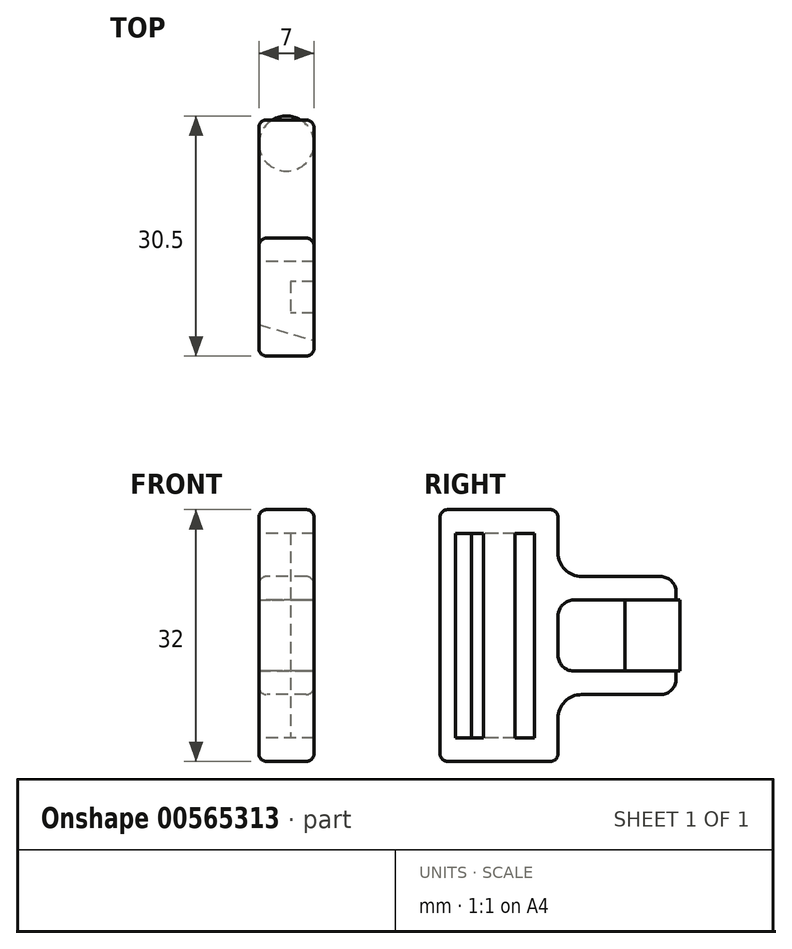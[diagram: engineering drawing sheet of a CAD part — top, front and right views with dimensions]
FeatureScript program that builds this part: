
annotation { "Feature Type Name" : "Feature", "Feature Type Description" : "" }
export const myFeature = defineFeature(function(context is Context, id is Id, definition is map)
    precondition{}
    {
        {
            var Q0;
            Q0=qCreatedBy(makeId("Right.planeOp"),FACE);
            var sketch = newSketch(context, id + "F0", { "sketchPlane" : qUnion([Q0])});
            skLineSegment(sketch, "E0.bottom", {"start": v(3, 4.5) * mm, "end": v(-12, 4.5) * mm});
            skLineSegment(sketch, "E0.top", {"start": v(3, 7.5) * mm, "end": v(-12, 7.5) * mm});
            skLineSegment(sketch, "E0.left", {"start": v(3, 4.5) * mm, "end": v(3, 7.5) * mm});
            skLineSegment(sketch, "E0.right", {"start": v(-12, 4.5) * mm, "end": v(-12, 7.5) * mm});
            skLineSegment(sketch, "E1.bottom", {"start": v(3, -4.5) * mm, "end": v(-12, -4.5) * mm});
            skLineSegment(sketch, "E1.top", {"start": v(3, -7.5) * mm, "end": v(-12, -7.5) * mm});
            skLineSegment(sketch, "E1.left", {"start": v(3, -4.5) * mm, "end": v(3, -7.5) * mm});
            skLineSegment(sketch, "E1.right", {"start": v(-12, -4.5) * mm, "end": v(-12, -7.5) * mm});
            skLineSegment(sketch, "E2.bottom", {"start": v(-12, 16) * mm, "end": v(-27, 16) * mm});
            skLineSegment(sketch, "E2.top", {"start": v(-12, -16) * mm, "end": v(-27, -16) * mm});
            skLineSegment(sketch, "E2.left", {"start": v(-12, 16) * mm, "end": v(-12, -16) * mm});
            skLineSegment(sketch, "E2.right", {"start": v(-27, 16) * mm, "end": v(-27, -16) * mm});
            skLineSegment(sketch, "E3.bottom", {"start": v(-15, 13) * mm, "end": v(-17.5, 13) * mm});
            skLineSegment(sketch, "E3.top", {"start": v(-15, -13) * mm, "end": v(-17.5, -13) * mm});
            skLineSegment(sketch, "E3.left", {"start": v(-15, 13) * mm, "end": v(-15, -13) * mm});
            skLineSegment(sketch, "E3.right", {"start": v(-17.5, 13) * mm, "end": v(-17.5, -13) * mm});
            skPoint(sketch, "E4", {"position": v(-12, 0) * mm});
            skPoint(sketch, "E5", {"position": v(-15, 0) * mm});
            skLineSegment(sketch, "E6", {"start": v(0, 4.5) * mm, "end": v(0, -4.5) * mm, "construction": true});
            skPoint(sketch, "E7", {"position": v(0, 0) * mm});
            skLineSegment(sketch, "E8.bottom", {"start": v(-21.5, 13) * mm, "end": v(-23, 13) * mm});
            skLineSegment(sketch, "E8.top", {"start": v(-21.5, -13) * mm, "end": v(-23, -13) * mm});
            skLineSegment(sketch, "E8.left", {"start": v(-21.5, 13) * mm, "end": v(-21.5, -13) * mm});
            skLineSegment(sketch, "E8.right", {"start": v(-23, 13) * mm, "end": v(-23, -13) * mm});
            skSolve(sketch);
        }
        {
            var Q0;
            Q0=qSketchRegion(id+"F0",true);
            extrude(context, id + "F1", {"entities" : qUnion([Q0]), "endBound" : BoundingType.SYMMETRIC, "depth" : 7 * mm, "offsetDistance" : 25 * mm});
        }
        {
            var Q0;
            Q0=makeQuery(id+"F1.opExtrude","SWEPT_FACE",FACE,{"disambiguationData":[OSD([sQuery(id+"F0.wireOp",EDGE,"E1.bottom")])]});
            var sketch = newSketch(context, id + "F2", { "sketchPlane" : qUnion([Q0])});
            skCircle(sketch, "E9", {"center": v(0, 0) * mm, "radius": 3.5 * mm});
            skSolve(sketch);
        }
        {
            var Q0;
            Q0=qSketchRegion(id+"F2",true);
            var Q1;
            Q1=makeQuery(id+"F1.opExtrude","SWEPT_FACE",FACE,{"disambiguationData":[OSD([sQuery(id+"F0.wireOp",EDGE,"E0.bottom")])]});
            extrude(context, id + "F3", {"entities" : qUnion([Q0]), "operationType" : NewBodyOperationType.ADD, "endBound" : BoundingType.UP_TO_SURFACE, "depth" : 25 * mm, "endBoundEntityFace" : qUnion([Q1]), "offsetDistance" : 25 * mm});
        }
        {
            var Q0;
            Q0=makeQuery(id+"F1.opExtrude","SWEPT_EDGE",EDGE,{"disambiguationData":[OSD([sQuery(id+"F0.wireOp",EDGE,"E2.bottom"),sQuery(id+"F0.wireOp",EDGE,"E2.right")])]});
            var Q1;
            Q1=makeQuery(id+"F1.opExtrude","SWEPT_EDGE",EDGE,{"disambiguationData":[OSD([sQuery(id+"F0.wireOp",EDGE,"E2.bottom"),sQuery(id+"F0.wireOp",EDGE,"E2.left")])]});
            var Q2;
            Q2=makeQuery(id+"F1.opExtrude","SWEPT_EDGE",EDGE,{"disambiguationData":[OSD([sQuery(id+"F0.wireOp",EDGE,"E2.top"),sQuery(id+"F0.wireOp",EDGE,"E2.right")])]});
            var Q3;
            Q3=makeQuery(id+"F1.opExtrude","SWEPT_EDGE",EDGE,{"disambiguationData":[OSD([sQuery(id+"F0.wireOp",EDGE,"E2.top"),sQuery(id+"F0.wireOp",EDGE,"E2.left")])]});
            fillet(context, id + "F4", {"entities" : qUnion([Q0, Q1, Q2, Q3]), "radius" : 1 * mm, "tangentPropagation" : true, "allowEdgeOverflow" : false});
        }
        {
            var Q0;
            Q0=makeQuery(id+"F1.opExtrude","SWEPT_EDGE",EDGE,{"disambiguationData":[OSD([sQuery(id+"F0.wireOp",EDGE,"E0.top"),sQuery(id+"F0.wireOp",EDGE,"E2.left")])]});
            var Q1;
            Q1=makeQuery(id+"F1.opExtrude","SWEPT_EDGE",EDGE,{"disambiguationData":[OSD([sQuery(id+"F0.wireOp",EDGE,"E1.top"),sQuery(id+"F0.wireOp",EDGE,"E2.left")])]});
            fillet(context, id + "F5", {"entities" : qUnion([Q0, Q1]), "radius" : 3 * mm, "tangentPropagation" : true, "allowEdgeOverflow" : false});
        }
        {
            var Q0;
            Q0=makeQuery(id+"F1.opExtrude","SWEPT_EDGE",EDGE,{"disambiguationData":[OSD([sQuery(id+"F0.wireOp",EDGE,"E0.top"),sQuery(id+"F0.wireOp",EDGE,"E0.left")])]});
            var Q1;
            Q1=makeQuery(id+"F1.opExtrude","SWEPT_EDGE",EDGE,{"disambiguationData":[OSD([sQuery(id+"F0.wireOp",EDGE,"E1.top"),sQuery(id+"F0.wireOp",EDGE,"E1.left")])]});
            var Q2;
            Q2=makeQuery(id+"F1.opExtrude","SWEPT_EDGE",EDGE,{"disambiguationData":[OSD([sQuery(id+"F0.wireOp",EDGE,"E1.bottom"),sQuery(id+"F0.wireOp",EDGE,"E2.left")])]});
            var Q3;
            Q3=makeQuery(id+"F1.opExtrude","SWEPT_EDGE",EDGE,{"disambiguationData":[OSD([sQuery(id+"F0.wireOp",EDGE,"E0.bottom"),sQuery(id+"F0.wireOp",EDGE,"E2.left")])]});
            fillet(context, id + "F6", {"entities" : qUnion([Q0, Q1, Q2, Q3]), "radius" : 2 * mm, "tangentPropagation" : true, "allowEdgeOverflow" : false});
        }
        {
            var Q0;
            Q0=makeQuery(id+"F1.opExtrude","CAP_EDGE",EDGE,{"disambiguationData":[OSD([sQuery(id+"F0.wireOp",EDGE,"E1.top")])],"isStart":true});
            var Q1;
            Q1=makeQuery(id+"F1.opExtrude","CAP_EDGE",EDGE,{"disambiguationData":[OSD([sQuery(id+"F0.wireOp",EDGE,"E0.top")])],"isStart":true});
            var Q2;
            {var subQ0=sQuery(id+"F0.wireOp",EDGE,"E0.left");var subQ1=sQuery(id+"F0.wireOp",EDGE,"E0.top");Q2=makeQuery(id+"F6.opFillet","BLEND_EDGE",EDGE,{"blendedFrom":[makeQuery(id+"F1.opExtrude","SWEPT_EDGE",EDGE,{"disambiguationData":[OSD([subQ1,subQ0])]}),makeQuery(id+"F1.opExtrude","CAP_FACE",FACE,{"disambiguationData":[OSD([sQuery(id+"F0.wireOp",EDGE,"E0.bottom"),subQ1,subQ0,sQuery(id+"F0.wireOp",EDGE,"E1.bottom"),sQuery(id+"F0.wireOp",EDGE,"E1.top"),sQuery(id+"F0.wireOp",EDGE,"E1.left"),sQuery(id+"F0.wireOp",EDGE,"E2.bottom"),sQuery(id+"F0.wireOp",EDGE,"E2.top"),sQuery(id+"F0.wireOp",EDGE,"E2.left"),sQuery(id+"F0.wireOp",EDGE,"E2.right"),sQuery(id+"F0.wireOp",EDGE,"E3.bottom"),sQuery(id+"F0.wireOp",EDGE,"E3.top"),sQuery(id+"F0.wireOp",EDGE,"E3.left"),sQuery(id+"F0.wireOp",EDGE,"E3.right")])],"isStart":false})],"blendedInto":[makeQuery(id+"F1.opExtrude","CAP_FACE",FACE,{"disambiguationData":[OSD([sQuery(id+"F0.wireOp",EDGE,"E0.bottom"),subQ1,subQ0,sQuery(id+"F0.wireOp",EDGE,"E1.bottom"),sQuery(id+"F0.wireOp",EDGE,"E1.top"),sQuery(id+"F0.wireOp",EDGE,"E1.left"),sQuery(id+"F0.wireOp",EDGE,"E2.bottom"),sQuery(id+"F0.wireOp",EDGE,"E2.top"),sQuery(id+"F0.wireOp",EDGE,"E2.left"),sQuery(id+"F0.wireOp",EDGE,"E2.right"),sQuery(id+"F0.wireOp",EDGE,"E3.bottom"),sQuery(id+"F0.wireOp",EDGE,"E3.top"),sQuery(id+"F0.wireOp",EDGE,"E3.left"),sQuery(id+"F0.wireOp",EDGE,"E3.right")])],"isStart":false})]});}
            var Q3;
            {var subQ0=sQuery(id+"F0.wireOp",EDGE,"E1.left");var subQ1=sQuery(id+"F0.wireOp",EDGE,"E1.top");Q3=makeQuery(id+"F6.opFillet","BLEND_EDGE",EDGE,{"blendedFrom":[makeQuery(id+"F1.opExtrude","SWEPT_EDGE",EDGE,{"disambiguationData":[OSD([subQ1,subQ0])]}),makeQuery(id+"F1.opExtrude","CAP_FACE",FACE,{"disambiguationData":[OSD([sQuery(id+"F0.wireOp",EDGE,"E0.bottom"),sQuery(id+"F0.wireOp",EDGE,"E0.top"),sQuery(id+"F0.wireOp",EDGE,"E0.left"),sQuery(id+"F0.wireOp",EDGE,"E1.bottom"),subQ1,subQ0,sQuery(id+"F0.wireOp",EDGE,"E2.bottom"),sQuery(id+"F0.wireOp",EDGE,"E2.top"),sQuery(id+"F0.wireOp",EDGE,"E2.left"),sQuery(id+"F0.wireOp",EDGE,"E2.right"),sQuery(id+"F0.wireOp",EDGE,"E3.bottom"),sQuery(id+"F0.wireOp",EDGE,"E3.top"),sQuery(id+"F0.wireOp",EDGE,"E3.left"),sQuery(id+"F0.wireOp",EDGE,"E3.right")])],"isStart":false})],"blendedInto":[makeQuery(id+"F1.opExtrude","CAP_FACE",FACE,{"disambiguationData":[OSD([sQuery(id+"F0.wireOp",EDGE,"E0.bottom"),sQuery(id+"F0.wireOp",EDGE,"E0.top"),sQuery(id+"F0.wireOp",EDGE,"E0.left"),sQuery(id+"F0.wireOp",EDGE,"E1.bottom"),subQ1,subQ0,sQuery(id+"F0.wireOp",EDGE,"E2.bottom"),sQuery(id+"F0.wireOp",EDGE,"E2.top"),sQuery(id+"F0.wireOp",EDGE,"E2.left"),sQuery(id+"F0.wireOp",EDGE,"E2.right"),sQuery(id+"F0.wireOp",EDGE,"E3.bottom"),sQuery(id+"F0.wireOp",EDGE,"E3.top"),sQuery(id+"F0.wireOp",EDGE,"E3.left"),sQuery(id+"F0.wireOp",EDGE,"E3.right")])],"isStart":false})]});}
            fillet(context, id + "F7", {"entities" : qUnion([Q0, Q1, Q2, Q3]), "radius" : 1 * mm, "tangentPropagation" : true, "allowEdgeOverflow" : false});
        }
        {
            var Q0;
            Q0=makeQuery(id+"F1.opExtrude","CAP_EDGE",EDGE,{"disambiguationData":[OSD([sQuery(id+"F0.wireOp",EDGE,"E8.right")])],"isStart":false});
            chamfer(context, id + "F8", {"entities" : qUnion([Q0]), "chamferType" : ChamferType.TWO_OFFSETS, "width1" : 7 * mm, "oppositeDirection" : false, "width2" : 2 * mm, "tangentPropagation" : true});
        }
        {
            var Q0;
            Q0=makeQuery(id+"F1.opExtrude","CAP_FACE",FACE,{"disambiguationData":[OSD([sQuery(id+"F0.wireOp",EDGE,"E0.bottom"),sQuery(id+"F0.wireOp",EDGE,"E0.top"),sQuery(id+"F0.wireOp",EDGE,"E0.left"),sQuery(id+"F0.wireOp",EDGE,"E1.bottom"),sQuery(id+"F0.wireOp",EDGE,"E1.top"),sQuery(id+"F0.wireOp",EDGE,"E1.left"),sQuery(id+"F0.wireOp",EDGE,"E2.bottom"),sQuery(id+"F0.wireOp",EDGE,"E2.top"),sQuery(id+"F0.wireOp",EDGE,"E2.left"),sQuery(id+"F0.wireOp",EDGE,"E2.right"),sQuery(id+"F0.wireOp",EDGE,"E3.bottom"),sQuery(id+"F0.wireOp",EDGE,"E3.top"),sQuery(id+"F0.wireOp",EDGE,"E3.left"),sQuery(id+"F0.wireOp",EDGE,"E3.right"),sQuery(id+"F0.wireOp",EDGE,"E8.bottom"),sQuery(id+"F0.wireOp",EDGE,"E8.top"),sQuery(id+"F0.wireOp",EDGE,"E8.left"),sQuery(id+"F0.wireOp",EDGE,"E8.right")])],"isStart":true});
            var sketch = newSketch(context, id + "F9", { "sketchPlane" : qUnion([Q0])});
            skLineSegment(sketch, "E10.bottom", {"start": v(17.5, -13) * mm, "end": v(21.5, -13) * mm});
            skLineSegment(sketch, "E10.top", {"start": v(17.5, 13) * mm, "end": v(21.5, 13) * mm});
            skLineSegment(sketch, "E10.left", {"start": v(17.5, -13) * mm, "end": v(17.5, 13) * mm});
            skLineSegment(sketch, "E10.right", {"start": v(21.5, -13) * mm, "end": v(21.5, 13) * mm});
            skSolve(sketch);
        }
        {
            var Q0;
            Q0 = qSketchRegion(id + "F9", true);
            extrude(context, id + "F10", {"entities" : qUnion([Q0]), "operationType" : NewBodyOperationType.REMOVE, "oppositeDirection" : true, "depth" : 4 * mm, "offsetDistance" : 25 * mm});
        }
    });
